# Revit family: PRD_AR_WstBns_STRATOSFoldingSelfClosingLid_STRX608
name_source: partatom
category: Specialty Equipment
revit_build: Autodesk Revit 2018 (Build: 20190510_1515(x64)
units: mm (PartAtom-declared; Revit-internal decimal feet)

## family parameters
Always vertical = Yes
Cut with Voids When Loaded = No
OmniClass Number = 23.40.20.31
OmniClass Title = Refuse Disposal Furniture
Part Type = Normal
Room Calculation Point = No
Round Connector Dimension = Use Diameter
Shared = No
Work Plane-Based = No

## types (1)
- STRX608
    AssetType = Fixed
    BIMObjectName = PRD_AR_WasteBins_STRATOSFoldingSelfClosingLid_STRX608
    Category = Pr_40_50_07_96, Waste bins
    Color = no color
    Description = Folding self-closing lid for waste bin STRX607, stainless steel, surface satin finished, front with InoxPlus surface refinement for the reduction of finger marks and better cleaning characteristics (easy to clean), material thickness 1.5 mm, inclined front with selfclosing lid, cylinder lock with KWC standard key, includes stainless steel screws and dowels, without waste bin.
    DurationUnit = year
    Features = stainless steel, surface satin finished
    Finish = satin finished
    GrossWeight = 3.99 kg
    IfcExportAs = IfcFurnitureType
    IfcExportType = USERDEFINED
    IntegralAccessories = incl. stainless steel screws and dowels
    IsBuiltIn = TRUE
    Lock = Key-lock
    MainColor = stainless steel
    Manufacturer = KWC Group AG
    ManufacturerName = KWC Group AG
    ManufacturerURL = www.kwc.com
    Material = stainless steel
    MaterialCode = 1.4301
    MaterialThickness = 1.50 mm
    Model = STRX608
    ModelNumber = 2000057231
    ModelReference = STRX608
    NBSDescription = Waste bins
    NBSReference = 45-35-72/380
    Name = Folding Self Closing Lid STRX608
    NetWeight = 3.50 kg
    NominalDepth = 229 mm
    NominalHeight = 185 mm  [stored 0.606955 ft]
    NominalWidth = 399 mm  [stored 1.30906 ft]
    ProductInformation = https://pim.kwc.com
    Size = 399 x 185 x 229 mm
    SlotHeight = 120.00 mm
    SlotWidth = 264.00 mm
    SurfaceTreatment = InoxPlus (anti fingerprint)
    TypeOfFixing = Screw
    TypeOfMounting = On waste bin
    URL = www.kwc.com
    Uniclass2015Code = Pr_40_50_07_96
    Uniclass2015Title = Waste bins
    Uniclass2015Version = Products v1.10
    Version = 1
    WarrantyDurationUnit = year
    WasteBinMaterial = PRD_AR_StainlessSteel_SatinFinished_Perforated

note: [stored X ft] marks values corroborated as IEEE doubles in the binary element streams (Revit-internal decimal feet)

## geometry (parser evidence)
native form markers: Sweep x2
no freeform markers — native parametric forms only
